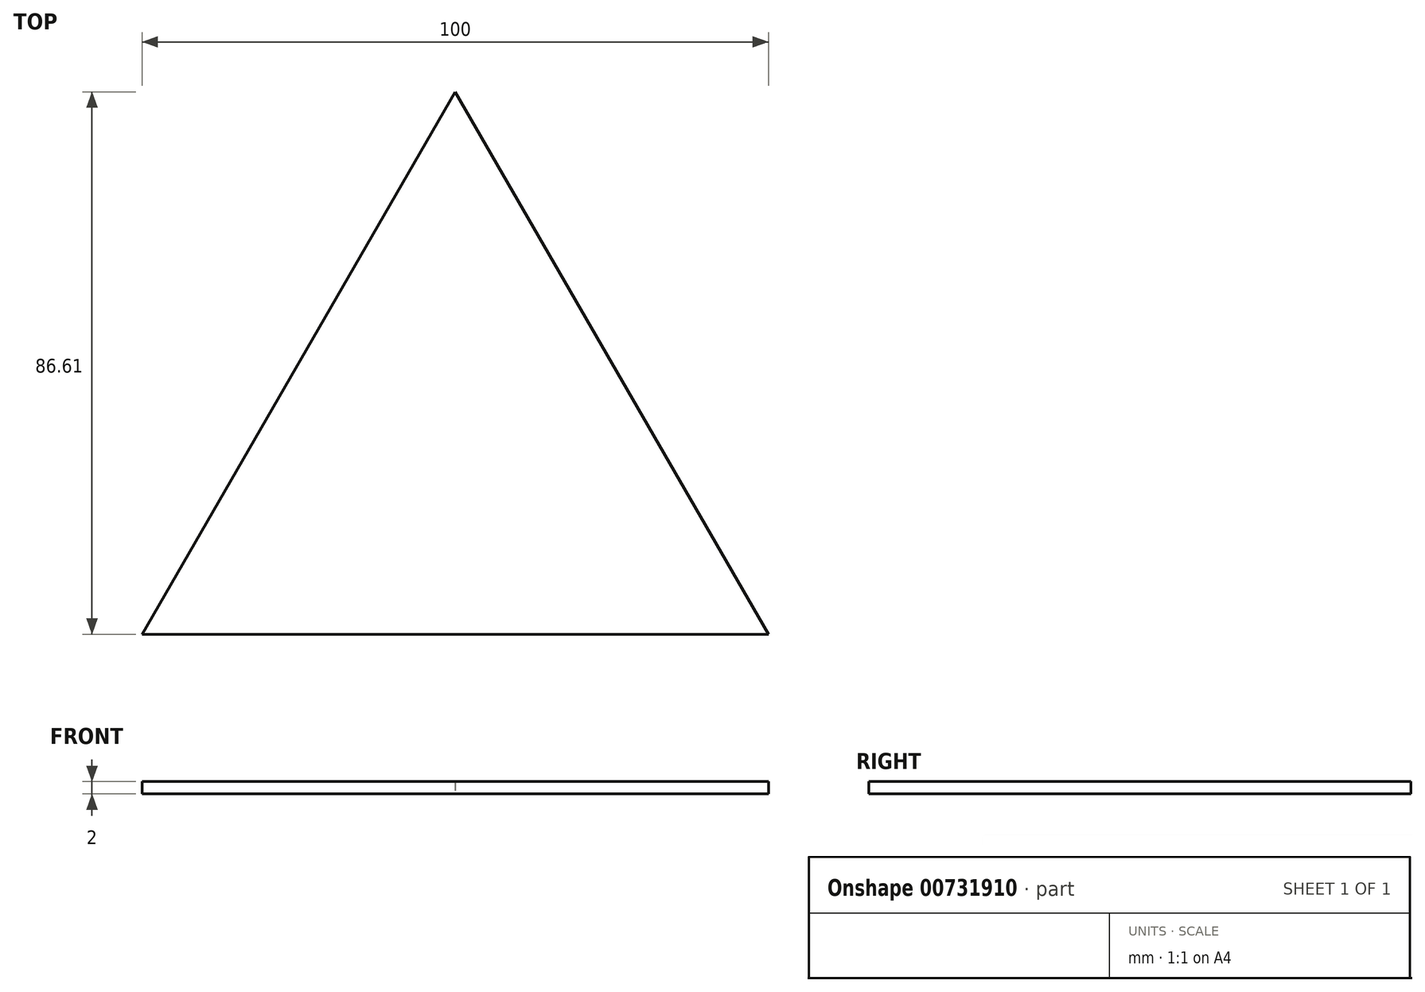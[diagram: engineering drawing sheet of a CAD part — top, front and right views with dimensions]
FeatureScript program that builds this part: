
annotation { "Feature Type Name" : "Feature", "Feature Type Description" : "" }
export const myFeature = defineFeature(function(context is Context, id is Id, definition is map)
    precondition{}
    {
        {
            var Q0;
            Q0=qCreatedBy(makeId("Top.planeOp"),FACE);
            var sketch = newSketch(context, id + "F0", { "sketchPlane" : qUnion([Q0])});
            skLineSegment(sketch, "E0", {"start": v(-50, -28.87) * mm, "end": v(50, -28.87) * mm});
            skLineSegment(sketch, "E1", {"start": v(50, -28.87) * mm, "end": v(0, 57.74) * mm});
            skLineSegment(sketch, "E2", {"start": v(0, 57.74) * mm, "end": v(-50, -28.87) * mm});
            skLineSegment(sketch, "E3", {"start": v(0, 57.74) * mm, "end": v(0, -28.87) * mm, "construction": true});
            skLineSegment(sketch, "E4", {"start": v(50, -28.87) * mm, "end": v(-25, 14.43) * mm, "construction": true});
            skSolve(sketch);
        }
        {
            var Q0;
            Q0 = qSketchRegion(id + "F0", true);
            extrude(context, id + "F1", {"entities" : qUnion([Q0]), "depth" : 2 * mm, "offsetDistance" : 25 * mm});
        }
    });
